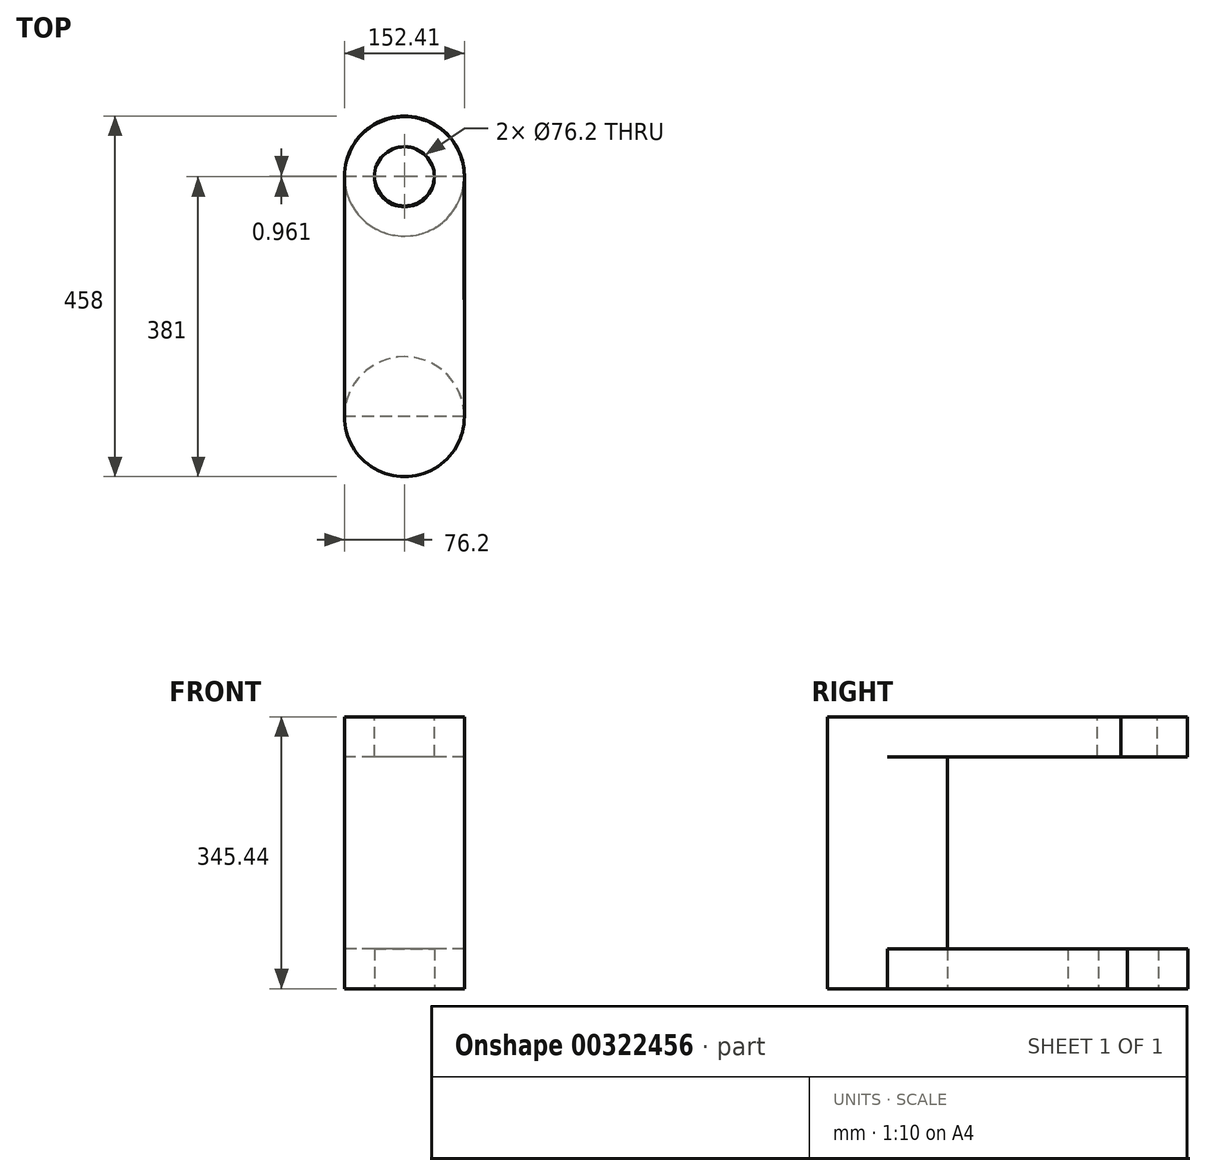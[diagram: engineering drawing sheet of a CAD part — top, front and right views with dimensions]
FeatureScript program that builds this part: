
annotation { "Feature Type Name" : "Feature", "Feature Type Description" : "" }
export const myFeature = defineFeature(function(context is Context, id is Id, definition is map)
    precondition{}
    {
        {
            var Q0;
            Q0=qCreatedBy(makeId("Top.planeOp"),FACE);
            var sketch = newSketch(context, id + "F0", { "sketchPlane" : qUnion([Q0])});
            skCircle(sketch, "E0", {"center": v(0, 0) * mm, "radius": 76.2 * mm});
            skSolve(sketch);
        }
        {
            var Q0;
            Q0=qCreatedBy(makeId("Top.planeOp"),FACE);
            var sketch = newSketch(context, id + "F1", { "sketchPlane" : qUnion([Q0])});
            skLineSegment(sketch, "E1", {"start": v(0, 0) * mm, "end": v(-76.19, 0) * mm});
            skLineSegment(sketch, "E2", {"start": v(-76.19, 0) * mm, "end": v(-76.19, 304.8) * mm});
            skLineSegment(sketch, "E3", {"start": v(0, 0) * mm, "end": v(76.21, 0) * mm});
            skLineSegment(sketch, "E4", {"start": v(76.21, 0) * mm, "end": v(76.21, 304.8) * mm});
            skLineSegment(sketch, "E5", {"start": v(76.21, 304.8) * mm, "end": v(-76.19, 304.8) * mm});
            skSolve(sketch);
        }
        {
            var Q0;
            Q0=makeQuery(id+"F1.imprint","IMPRINT",FACE,{"disambiguationData":[TD([[makeQuery(id+"F1.imprint","IMPRINT",EDGE,{"derivedFrom":sQuery(id+"F1.wireOp",EDGE,"E1")}),-1.0]])]});
            var sketch = newSketch(context, id + "F2", { "sketchPlane" : qUnion([Q0])});
            skCircle(sketch, "E6", {"center": v(0, 305.6) * mm, "radius": 76.2 * mm});
            skSolve(sketch);
        }
        {
            var Q0;
            {var subQ1=makeQuery(id+"F1.imprint","IMPRINT",EDGE,{"derivedFrom":sQuery(id+"F1.wireOp",EDGE,"E1")});Q0=makeQuery(id+"F2.imprint","IMPRINT",FACE,{"disambiguationData":[TD([[makeQuery(id+"F2.imprint","IMPRINT",EDGE,{"derivedFrom":subQ1}),-1.0]])]});}
            var sketch = newSketch(context, id + "F3", { "sketchPlane" : qUnion([Q0])});
            skCircle(sketch, "E7", {"center": v(0, 0) * mm, "radius": 38.1 * mm});
            skCircle(sketch, "E8", {"center": v(0, 305.76) * mm, "radius": 38.1 * mm});
            skSolve(sketch);
        }
        {
            var Q0;
            Q0=makeQuery(id+"F0.imprint","IMPRINT",FACE,{"disambiguationData":[TD([[makeQuery(id+"F0.imprint","IMPRINT",EDGE,{"derivedFrom":sQuery(id+"F0.wireOp",EDGE,"E0")}),1.0]])]});
            extrude(context, id + "F4", {"entities" : qUnion([Q0]), "depth" : 345.44 * mm});
        }
        {
            var Q0;
            Q0=makeQuery(id+"F4.opExtrude","CAP_FACE",FACE,{"disambiguationData":[OSD([sQuery(id+"F0.wireOp",EDGE,"E0")])],"isStart":false});
            var sketch = newSketch(context, id + "F5", { "sketchPlane" : qUnion([Q0])});
            skCircle(sketch, "E9", {"center": v(0, 0) * mm, "radius": 76.2 * mm});
            skLineSegment(sketch, "E10", {"start": v(-76.2, 0) * mm, "end": v(-76.2, 304.8) * mm});
            skLineSegment(sketch, "E11", {"start": v(-76.2, 304.8) * mm, "end": v(75.72, 304.8) * mm});
            skLineSegment(sketch, "E12", {"start": v(75.72, 304.8) * mm, "end": v(76.2, 0) * mm});
            skLineSegment(sketch, "E13", {"start": v(76.2, 0) * mm, "end": v(-76.2, 0) * mm});
            skCircle(sketch, "E14", {"center": v(0, 304.8) * mm, "radius": 76.2 * mm});
            skCircle(sketch, "E15", {"center": v(0, 304.8) * mm, "radius": 38.1 * mm});
            skCircle(sketch, "E16", {"center": v(0, 0) * mm, "radius": 38.1 * mm});
            skSolve(sketch);
        }
        {
            var Q0;
            {var subQ1=sQuery(id+"F5.wireOp",EDGE,"E11");var subQ3=sQuery(id+"F5.wireOp",EDGE,"E12");var subQ5=makeQuery(id+"F5.imprint","INTERSECT",VERTEX,{"derivedFrom":[subQ1,subQ3]});Q0=makeQuery(id+"F5.imprint","IMPRINT",FACE,{"disambiguationData":[TD([[makeQuery(id+"F5.imprint","IMPRINT",EDGE,{"disambiguationData":[TD([[subQ5,1.0]])],"derivedFrom":subQ1}),-1.0]])]});}
            var Q1;
            {var subQ1=sQuery(id+"F5.wireOp",EDGE,"E11");var subQ3=sQuery(id+"F5.wireOp",EDGE,"E12");var subQ5=makeQuery(id+"F5.imprint","INTERSECT",VERTEX,{"derivedFrom":[subQ1,subQ3]});Q1=makeQuery(id+"F5.imprint","IMPRINT",FACE,{"disambiguationData":[TD([[makeQuery(id+"F5.imprint","IMPRINT",EDGE,{"disambiguationData":[TD([[subQ5,1.0]])],"derivedFrom":subQ1}),1.0]])]});}
            var Q2;
            {var subQ0=sQuery(id+"F5.wireOp",EDGE,"E10");Q2=makeQuery(id+"F5.imprint","IMPRINT",FACE,{"disambiguationData":[TD([[makeQuery(id+"F5.imprint","IMPRINT",EDGE,{"derivedFrom":subQ0}),-1.0]])]});}
            extrude(context, id + "F6", {"entities" : qUnion([Q0, Q1, Q2]), "operationType" : NewBodyOperationType.ADD, "oppositeDirection" : true, "depth" : 50.8 * mm});
        }
        {
            var Q0;
            {var subQ0=sQuery(id+"F2.wireOp",EDGE,"E6");var subQ1=makeQuery(id+"F1.imprint","IMPRINT",EDGE,{"derivedFrom":sQuery(id+"F1.wireOp",EDGE,"E2")});var subQ2=makeQuery(id+"F2.imprint","INTERSECT",VERTEX,{"derivedFrom":[subQ1,subQ0]});Q0=makeQuery(id+"F2.imprint","IMPRINT",FACE,{"disambiguationData":[TD([[makeQuery(id+"F2.imprint","IMPRINT",EDGE,{"disambiguationData":[TD([[subQ2,-1.0]])],"derivedFrom":subQ0}),1.0]])]});}
            var Q1;
            {var subQ0=sQuery(id+"F2.wireOp",EDGE,"E6");var subQ1=makeQuery(id+"F1.imprint","IMPRINT",EDGE,{"derivedFrom":sQuery(id+"F1.wireOp",EDGE,"E2")});var subQ2=makeQuery(id+"F2.imprint","INTERSECT",VERTEX,{"derivedFrom":[subQ1,subQ0]});Q1=makeQuery(id+"F2.imprint","IMPRINT",FACE,{"disambiguationData":[TD([[makeQuery(id+"F2.imprint","IMPRINT",EDGE,{"disambiguationData":[TD([[subQ2,1.0]])],"derivedFrom":subQ0}),1.0]])]});}
            var Q2;
            Q2=makeQuery(id+"F1.imprint","IMPRINT",FACE,{"disambiguationData":[TD([[makeQuery(id+"F1.imprint","IMPRINT",EDGE,{"derivedFrom":sQuery(id+"F1.wireOp",EDGE,"E1")}),-1.0]])]});
            extrude(context, id + "F7", {"entities" : qUnion([Q0, Q1, Q2]), "depth" : 50.8 * mm});
        }
        {
            var Q0;
            Q0=makeQuery(id+"F3.imprint","IMPRINT",FACE,{"disambiguationData":[TD([[makeQuery(id+"F3.imprint","IMPRINT",EDGE,{"derivedFrom":sQuery(id+"F3.wireOp",EDGE,"E8")}),1.0]])]});
            var Q1;
            Q1=sQuery(id+"F3.wireOp",EDGE,"E8");
            extrude(context, id + "F8", {"entities" : qUnion([Q0]), "operationType" : NewBodyOperationType.REMOVE, "surfaceEntities" : qUnion([Q1]), "depth" : 91.44 * mm});
        }
    });
